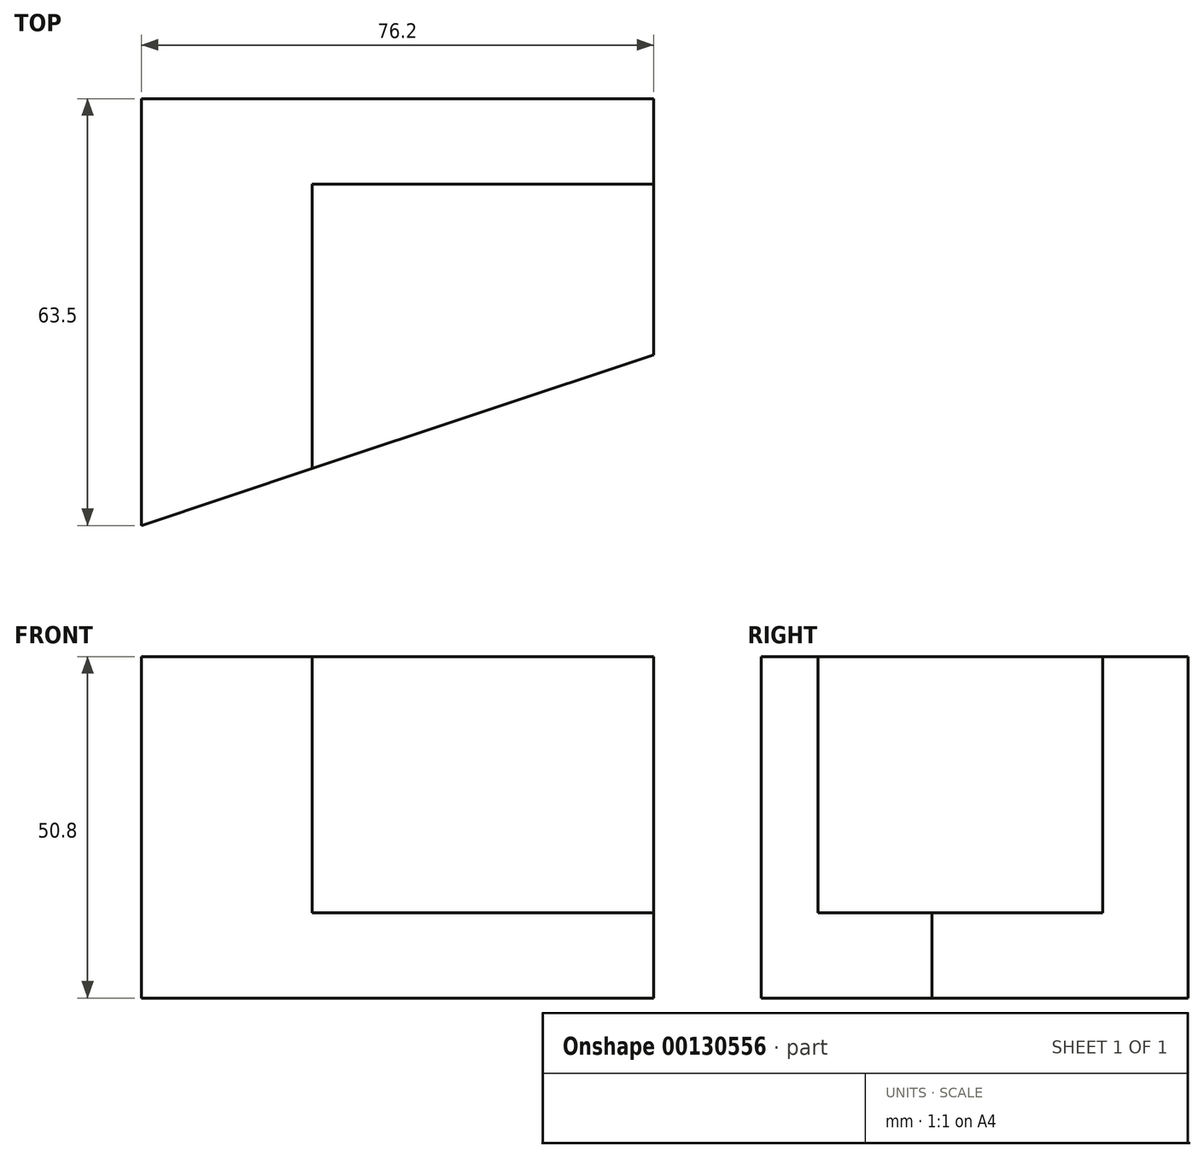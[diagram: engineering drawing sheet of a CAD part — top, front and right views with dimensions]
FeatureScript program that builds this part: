
annotation { "Feature Type Name" : "Feature", "Feature Type Description" : "" }
export const myFeature = defineFeature(function(context is Context, id is Id, definition is map)
    precondition{}
    {
        {
            var Q0;
            Q0=qCreatedBy(makeId("Front.planeOp"),FACE);
            var sketch = newSketch(context, id + "F0", { "sketchPlane" : qUnion([Q0])});
            skLineSegment(sketch, "E0.bottom", {"start": v(0, 0) * mm, "end": v(76.2, 0) * mm});
            skLineSegment(sketch, "E0.top", {"start": v(0, 50.8) * mm, "end": v(76.2, 50.8) * mm});
            skLineSegment(sketch, "E0.left", {"start": v(0, 0) * mm, "end": v(0, 50.8) * mm});
            skLineSegment(sketch, "E0.right", {"start": v(76.2, 0) * mm, "end": v(76.2, 50.8) * mm});
            skSolve(sketch);
        }
        {
            var Q0;
            Q0=makeQuery(id+"F0.imprint","IMPRINT",FACE,{"disambiguationData":[TD([[makeQuery(id+"F0.imprint","IMPRINT",EDGE,{"derivedFrom":sQuery(id+"F0.wireOp",EDGE,"E0.bottom")}),1.0]])]});
            extrude(context, id + "F1", {"entities" : qUnion([Q0]), "oppositeDirection" : true, "depth" : 63.5 * mm});
        }
        {
            var Q0;
            Q0=makeQuery(id+"F1.opExtrude","SWEPT_FACE",FACE,{"disambiguationData":[OSD([sQuery(id+"F0.wireOp",EDGE,"E0.top")])]});
            var sketch = newSketch(context, id + "F2", { "sketchPlane" : qUnion([Q0])});
            skLineSegment(sketch, "E1", {"start": v(0, 0) * mm, "end": v(76.2, 25.4) * mm});
            skLineSegment(sketch, "E2", {"start": v(76.2, 25.4) * mm, "end": v(76.2, 0) * mm});
            skLineSegment(sketch, "E3", {"start": v(76.2, 0) * mm, "end": v(0, 0) * mm});
            skSolve(sketch);
        }
        {
            var Q0;
            Q0=makeQuery(id+"F2.imprint","IMPRINT",FACE,{"disambiguationData":[TD([[makeQuery(id+"F2.imprint","IMPRINT",EDGE,{"derivedFrom":sQuery(id+"F2.wireOp",EDGE,"E1")}),-1.0]])]});
            extrude(context, id + "F3", {"entities" : qUnion([Q0]), "operationType" : NewBodyOperationType.REMOVE, "endBound" : BoundingType.THROUGH_ALL, "oppositeDirection" : true, "depth" : 25.4 * mm});
        }
        {
            var Q0;
            Q0=makeQuery(id+"F1.opExtrude","SWEPT_FACE",FACE,{"disambiguationData":[OSD([sQuery(id+"F0.wireOp",EDGE,"E0.top")])]});
            var sketch = newSketch(context, id + "F4", { "sketchPlane" : qUnion([Q0])});
            skLineSegment(sketch, "E4.bottom", {"start": v(76.2, 0) * mm, "end": v(25.4, 0) * mm});
            skLineSegment(sketch, "E4.top", {"start": v(76.2, 50.8) * mm, "end": v(25.4, 50.8) * mm});
            skLineSegment(sketch, "E4.left", {"start": v(76.2, 0) * mm, "end": v(76.2, 50.8) * mm});
            skLineSegment(sketch, "E4.right", {"start": v(25.4, 0) * mm, "end": v(25.4, 50.8) * mm});
            skSolve(sketch);
        }
        {
            var Q0;
            {var subQ0=sQuery(id+"F4.wireOp",EDGE,"E4.top");Q0=makeQuery(id+"F4.imprint","IMPRINT",FACE,{"disambiguationData":[TD([[makeQuery(id+"F4.imprint","IMPRINT",EDGE,{"derivedFrom":subQ0}),1.0]])]});}
            extrude(context, id + "F5", {"entities" : qUnion([Q0]), "operationType" : NewBodyOperationType.REMOVE, "oppositeDirection" : true, "depth" : 38.1 * mm});
        }
    });
